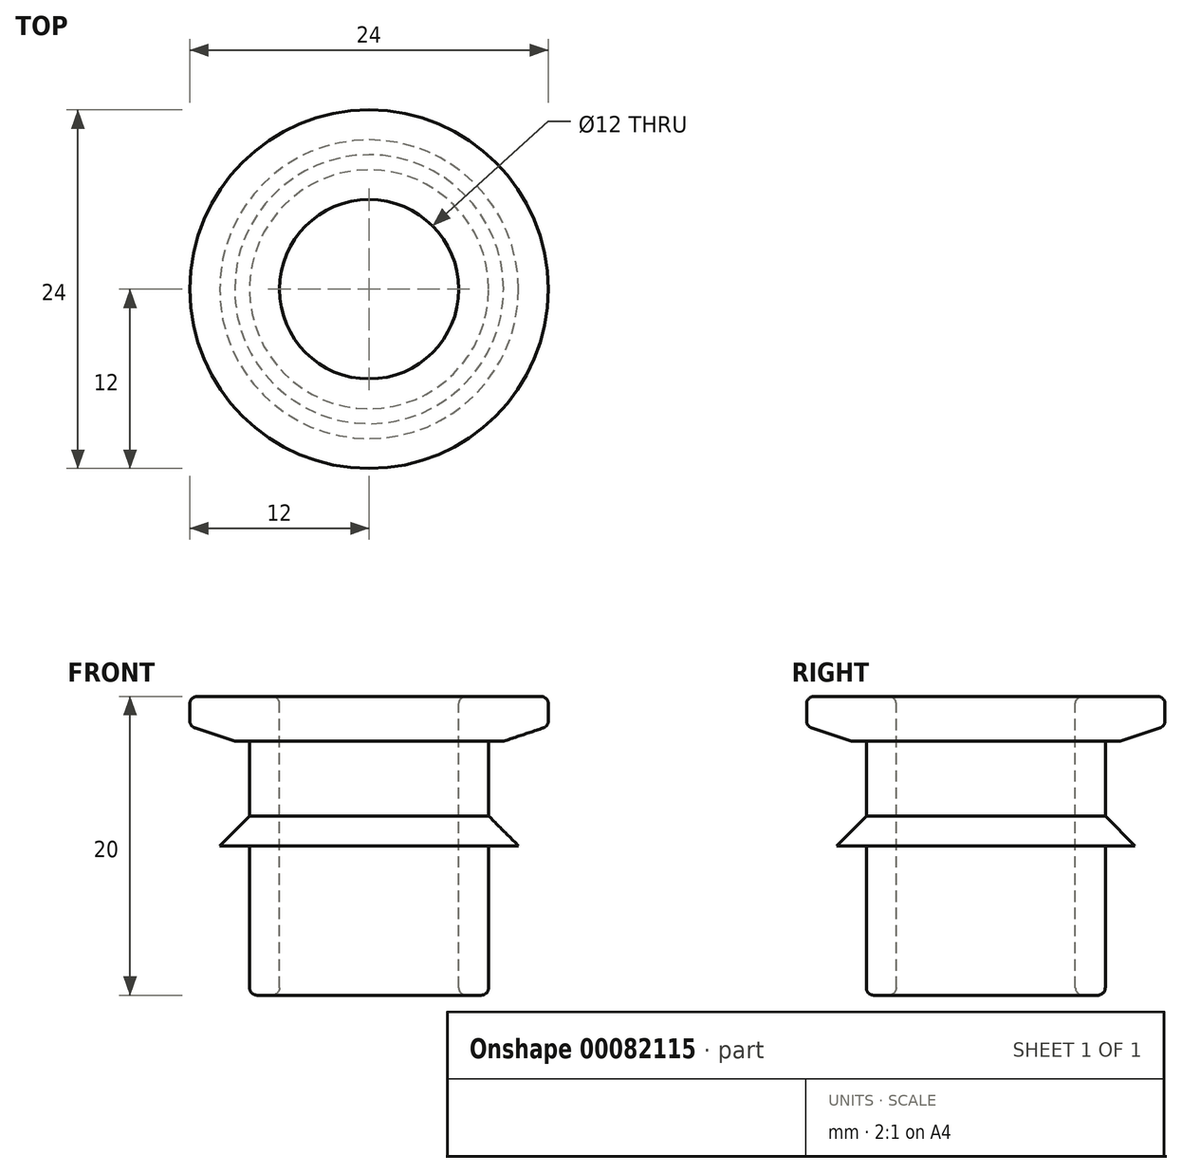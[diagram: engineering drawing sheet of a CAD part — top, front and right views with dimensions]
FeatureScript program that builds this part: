
annotation { "Feature Type Name" : "Feature", "Feature Type Description" : "" }
export const myFeature = defineFeature(function(context is Context, id is Id, definition is map)
    precondition{}
    {
        {
            var Q0;
            Q0=qCreatedBy(makeId("Top.planeOp"),FACE);
            var sketch = newSketch(context, id + "F0", { "sketchPlane" : qUnion([Q0])});
            skCircle(sketch, "E0", {"center": v(0, 0) * mm, "radius": 8 * mm});
            skCircle(sketch, "E1", {"center": v(0, 0) * mm, "radius": 6 * mm});
            skSolve(sketch);
        }
        {
            var Q0;
            Q0 = qSketchRegion(id + "F0", true);
            extrude(context, id + "F1", {"entities" : qUnion([Q0]), "oppositeDirection" : true, "depth" : 10 * mm});
        }
        {
            var Q0;
            Q0=qCreatedBy(makeId("Top.planeOp"),FACE);
            var sketch = newSketch(context, id + "F2", { "sketchPlane" : qUnion([Q0])});
            skCircle(sketch, "E2.0", {"center": v(0, 0) * mm, "radius": 6 * mm});
            skCircle(sketch, "E3", {"center": v(0, 0) * mm, "radius": 10 * mm});
            skSolve(sketch);
        }
        {
            var Q0;
            Q0 = qSketchRegion(id + "F2", true);
            extrude(context, id + "F3", {"entities" : qUnion([Q0]), "operationType" : NewBodyOperationType.ADD, "depth" : 2 * mm});
        }
        {
            var Q0;
            Q0=makeQuery(id+"F3.opExtrude","CAP_FACE",FACE,{"disambiguationData":[OSD([sQuery(id+"F2.wireOp",EDGE,"E2.0"),sQuery(id+"F2.wireOp",EDGE,"E3")])],"isStart":false});
            var sketch = newSketch(context, id + "F4", { "sketchPlane" : qUnion([Q0])});
            skCircle(sketch, "E4.0", {"center": v(0, 0) * mm, "radius": 6 * mm});
            skCircle(sketch, "E5", {"center": v(0, 0) * mm, "radius": 8 * mm});
            skSolve(sketch);
        }
        {
            var Q0;
            Q0 = qSketchRegion(id + "F4", true);
            extrude(context, id + "F5", {"entities" : qUnion([Q0]), "operationType" : NewBodyOperationType.ADD, "depth" : 5 * mm});
        }
        {
            var Q0;
            Q0=makeQuery(id+"F5.opExtrude","CAP_FACE",FACE,{"disambiguationData":[OSD([sQuery(id+"F4.wireOp",EDGE,"E4.0"),sQuery(id+"F4.wireOp",EDGE,"E5")])],"isStart":false});
            var sketch = newSketch(context, id + "F6", { "sketchPlane" : qUnion([Q0])});
            skCircle(sketch, "E6.0", {"center": v(0, 0) * mm, "radius": 6 * mm});
            skCircle(sketch, "E7", {"center": v(0, 0) * mm, "radius": 12 * mm});
            skSolve(sketch);
        }
        {
            var Q0;
            Q0 = qSketchRegion(id + "F6", true);
            extrude(context, id + "F7", {"entities" : qUnion([Q0]), "operationType" : NewBodyOperationType.ADD, "depth" : 3 * mm});
        }
        {
            var Q0;
            Q0=makeQuery(id+"F3.opExtrude","CAP_EDGE",EDGE,{"disambiguationData":[OSD([sQuery(id+"F2.wireOp",EDGE,"E3")])],"isStart":false});
            chamfer(context, id + "F8", {"entities" : qUnion([Q0]), "width" : 2 * mm, "tangentPropagation" : true});
        }
        {
            var Q0;
            Q0=makeQuery(id+"F7.opExtrude","CAP_EDGE",EDGE,{"disambiguationData":[OSD([sQuery(id+"F6.wireOp",EDGE,"E7")])],"isStart":true});
            chamfer(context, id + "F9", {"entities" : qUnion([Q0]), "chamferType" : ChamferType.TWO_OFFSETS, "width1" : 1 * mm, "oppositeDirection" : false, "width2" : 3 * mm, "tangentPropagation" : true});
        }
        {
            var Q0;
            Q0=makeQuery(id+"F7.opExtrude","SWEPT_FACE",FACE,{"disambiguationData":[OSD([sQuery(id+"F6.wireOp",EDGE,"E7")])]});
            var Q1;
            Q1=makeQuery(id+"F7.boolean.opBoolean","MERGE",FACE,{"derivedFrom":[makeQuery(id+"F5.boolean.opBoolean","MERGE",FACE,{"derivedFrom":[makeQuery(id+"F3.boolean.opBoolean","MERGE",FACE,{"derivedFrom":[makeQuery(id+"F1.opExtrude","SWEPT_FACE",FACE,{"disambiguationData":[OSD([sQuery(id+"F0.wireOp",EDGE,"E1")])]}),makeQuery(id+"F3.opExtrude","SWEPT_FACE",FACE,{"disambiguationData":[OSD([sQuery(id+"F2.wireOp",EDGE,"E2.0")])]})]}),makeQuery(id+"F5.opExtrude","SWEPT_FACE",FACE,{"disambiguationData":[OSD([sQuery(id+"F4.wireOp",EDGE,"E4.0")])]})]}),makeQuery(id+"F7.opExtrude","SWEPT_FACE",FACE,{"disambiguationData":[OSD([sQuery(id+"F6.wireOp",EDGE,"E6.0")])]})]});
            var Q2;
            Q2=makeQuery(id+"F1.opExtrude","CAP_EDGE",EDGE,{"disambiguationData":[OSD([sQuery(id+"F0.wireOp",EDGE,"E0")])],"isStart":false});
            fillet(context, id + "F10", {"entities" : qUnion([Q0, Q1, Q2]), "radius" : 0.5 * mm, "tangentPropagation" : true, "allowEdgeOverflow" : false});
        }
    });
